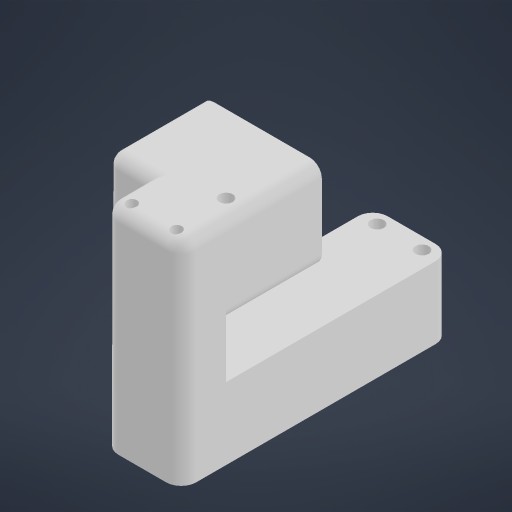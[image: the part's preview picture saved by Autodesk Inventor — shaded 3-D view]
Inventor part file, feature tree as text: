
AUTODESK INVENTOR PART (.ipt)
format: ipt  version: 2024.1 (Build 281209000, 209)  size: 377,856 bytes
history: native  units: mm
features: extrude x13, sketch x6, fillet x3, projected_geometry x3
ambient origin geometry x8: Origin, YZ Plane, XZ Plane, XY Plane, X Axis, Y Axis, Z Axis, Center Point
bodies: Solid1 (feature_tree)
feature tree (25):
  sketch  "Sketch1"  dims[d0=22.0mm d1=70.0mm]
  extrude  "Extrusion1"  Depth=70.0mm
  extrude  "Extrusion2"  Depth=2.0mm
  extrude  "Extrusion3"  Depth=15.0mm
  fillet  "Fillet1"  Radius=2.0mm
  sketch  "Sketch2"  dims[d2=2.0mm d3=4.5mm]
  extrude  "Extrusion4"  Depth=8.0mm
  sketch  "Sketch3"  dims[d4=8.0mm d6=15.0mm d7=2.0mm d8=0.0mm]
  extrude  "Extrusion5"  Depth=8.0mm TaperAngle=0.0deg
  extrude  "Extrusion6"  Depth=3.5mm
  sketch  "Sketch5"  dims[d9=22.0mm d10=0.0mm d11=8.0mm]
  extrude  "Extrusion8"  Depth=15.0mm
  extrude  "Extrusion13"  Depth=47.0mm TaperAngle=0.0deg
  extrude  "Extrusion14"  Depth=40.0mm
  extrude  "Extrusion15"  Depth=30.0mm
  extrude  "Extrusion9"  Depth=2.0mm
  extrude  "Extrusion10"  Depth=2.0mm TaperAngle=0.0deg
  extrude  "Extrusion12"  Depth=30.0mm TaperAngle=0.0deg
  fillet  "Fillet2"  Radius=4.5mm
  fillet  "Fillet3"  Radius=2.0mm
  projected_geometry  "Projected Loop1"
  projected_geometry  "Projected Loop2"
  sketch  "Sketch6"  dims[d12=8.0mm d13=34.25mm d14=0.0mm]
  projected_geometry  "Projected Loop3"
  sketch  "Sketch7"  dims[d15=5.0mm d16=3.5mm d17=15.0mm d18=47.0mm d19=0.0mm d23=40.0mm d26=30.0mm d27=2.0mm d28=2.0mm d29=0.0mm d30=30.0mm d31=0.0mm d32=4.5mm d33=2.0mm d36=2.0mm d37=4.5mm d38=10.0mm d39=0.0mm d40=10.0mm d41=0.0mm d42=10.0mm d43=10.0mm d44=0.0mm d47=2.0mm d48=0.0mm d49=4.0mm d50=4.0mm d51=10.0mm d52=0.0mm d53=10.0mm d54=0.0mm d55=30.0mm d56=0.0mm]
